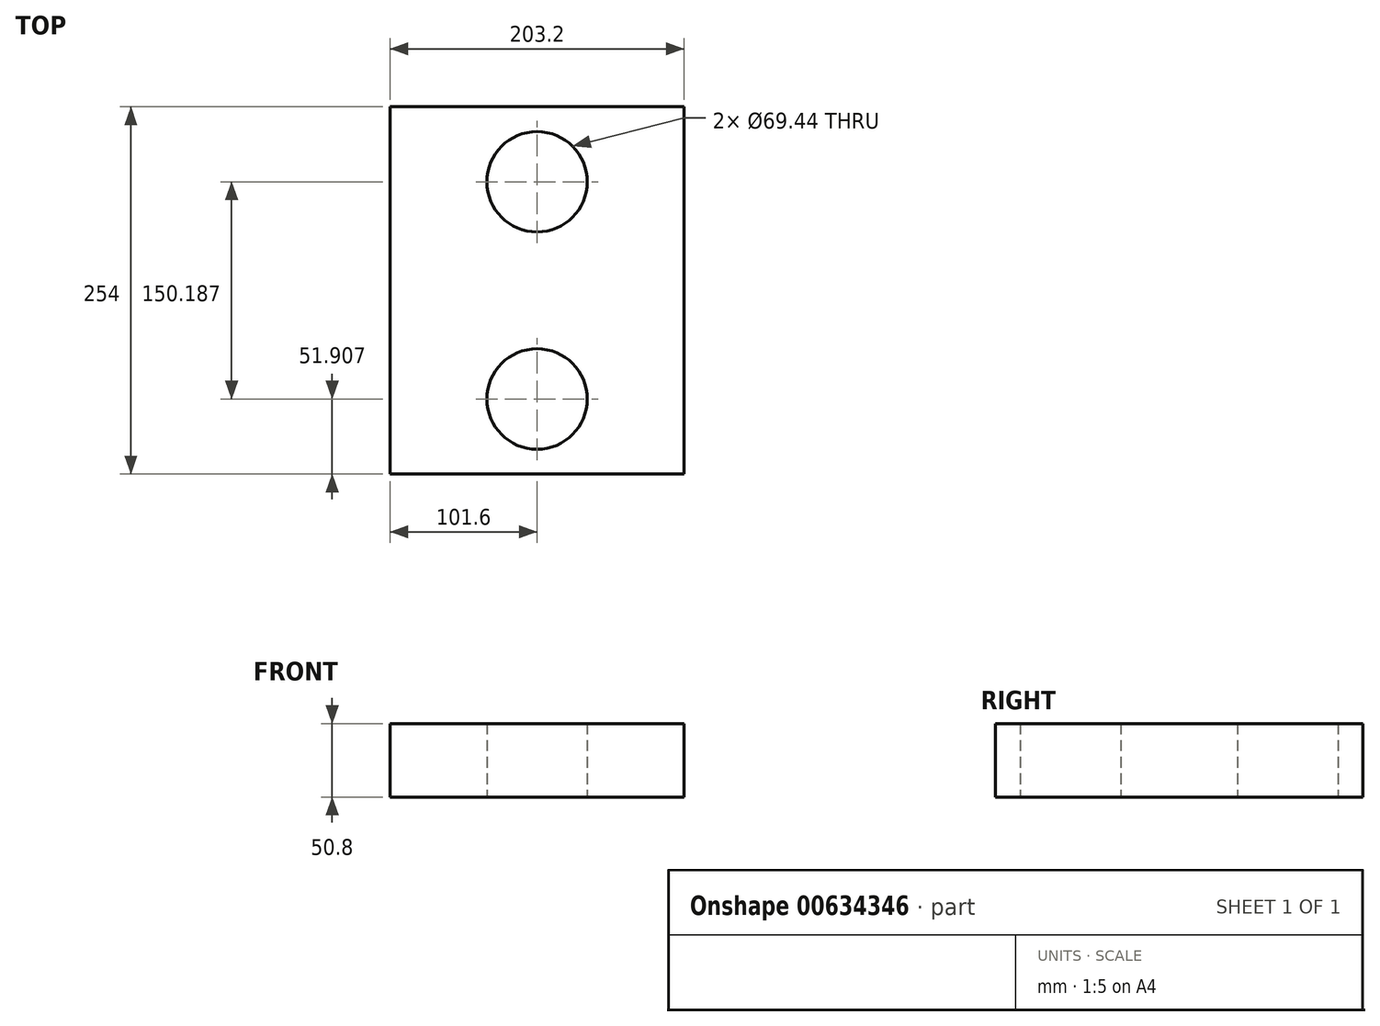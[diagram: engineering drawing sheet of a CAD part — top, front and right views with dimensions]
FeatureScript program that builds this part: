
annotation { "Feature Type Name" : "Feature", "Feature Type Description" : "" }
export const myFeature = defineFeature(function(context is Context, id is Id, definition is map)
    precondition{}
    {
        {
            var Q0;
            Q0=qCreatedBy(makeId("Top.planeOp"),FACE);
            var sketch = newSketch(context, id + "F0", { "sketchPlane" : qUnion([Q0])});
            skLineSegment(sketch, "E0.bottom", {"start": v(0, 0) * mm, "end": v(203.2, 0) * mm});
            skLineSegment(sketch, "E0.top", {"start": v(0, 254) * mm, "end": v(203.2, 254) * mm});
            skLineSegment(sketch, "E0.left", {"start": v(0, 0) * mm, "end": v(0, 254) * mm});
            skLineSegment(sketch, "E0.right", {"start": v(203.2, 0) * mm, "end": v(203.2, 254) * mm});
            skCircle(sketch, "E1", {"center": v(101.6, 202.1) * mm, "radius": 34.72 * mm});
            skPoint(sketch, "E1.centerSnap0", {"position": v(101.6, 0) * mm});
            skLineSegment(sketch, "E2", {"start": v(0, 127) * mm, "end": v(203.2, 127) * mm, "construction": true});
            skCircle(sketch, "E3.MirrorC", {"center": v(101.6, 51.9) * mm, "radius": 34.72 * mm});
            skSolve(sketch);
        }
        {
            var Q0;
            Q0=makeQuery(id+"F0.imprint","IMPRINT",FACE,{"disambiguationData":[TD([[makeQuery(id+"F0.imprint","IMPRINT",EDGE,{"derivedFrom":sQuery(id+"F0.wireOp",EDGE,"E0.bottom")}),1.0]])]});
            extrude(context, id + "F1", {"entities" : qUnion([Q0]), "depth" : 50.8 * mm, "offsetDistance" : 25.4 * mm});
        }
    });
